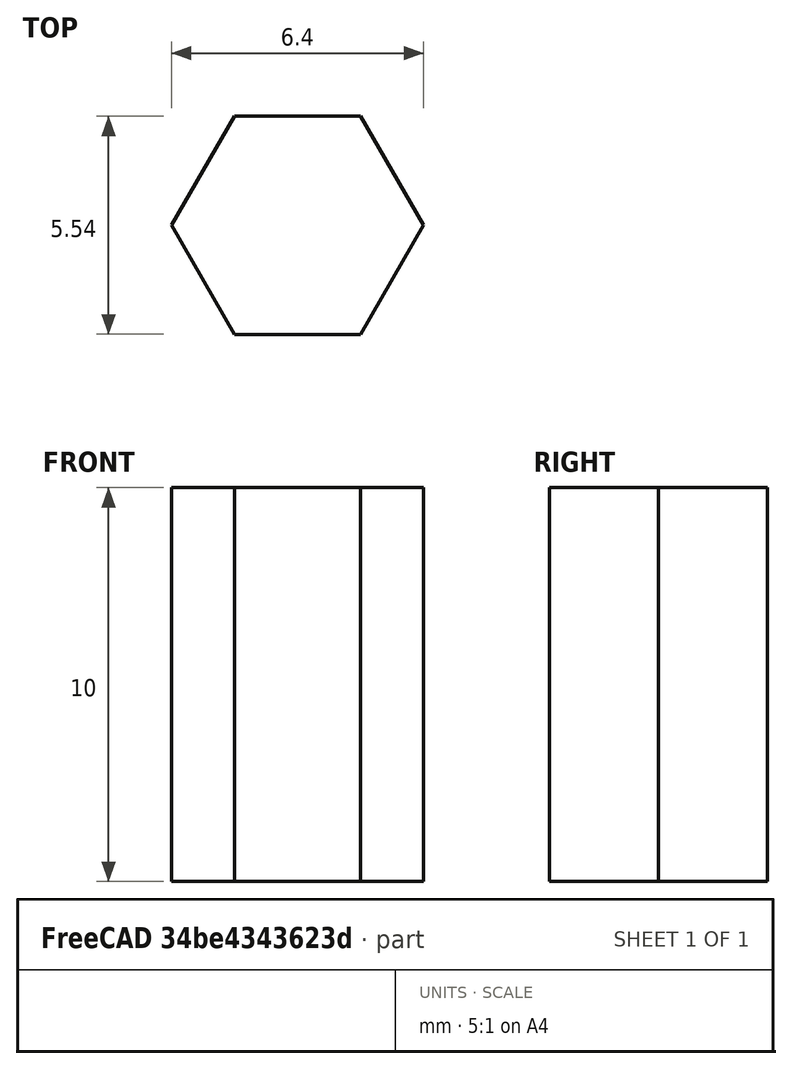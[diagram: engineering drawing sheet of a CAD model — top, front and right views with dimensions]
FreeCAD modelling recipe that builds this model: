
FCSTD DOCUMENT
Label: nut_trap
License: CC-BY 3.0
LicenseURL: http://creativecommons.org/licenses/by/3.0/
objects: Sketcher::SketchObject×1, Part::Extrusion×1
note: 2 computed .brp shape members not serialized (recipe doc carries the construction recipe); baked Part::Feature solids carry a one-line shape summary decoded from their .brp

FEATURE [Sketcher::SketchObject] Sketch
  sketch-geometry (7):
    g0: LineSegment StartX=-1.6 StartY=2.77128 StartZ=0 EndX=1.6 EndY=2.77128 EndZ=0
    g1: LineSegment StartX=1.6 StartY=2.77128 StartZ=0 EndX=3.2 EndY=0 EndZ=0
    g2: LineSegment StartX=3.2 StartY=0 StartZ=0 EndX=1.6 EndY=-2.77128 EndZ=0
    g3: LineSegment StartX=1.6 StartY=-2.77128 StartZ=0 EndX=-1.6 EndY=-2.77128 EndZ=0
    g4: LineSegment StartX=-1.6 StartY=-2.77128 StartZ=0 EndX=-3.2 EndY=0 EndZ=0
    g5: LineSegment StartX=-3.2 StartY=0 StartZ=0 EndX=-1.6 EndY=2.77128 EndZ=0
    g6: GeomPoint [constr] X=0 Y=0 Z=0
  constraints (19):
    c: Coincident(g0,g1)
    c: Coincident(g1,g2)
    c: Coincident(g2,g3)
    c: Coincident(g3,g4)
    c: Coincident(g4,g5)
    c: Coincident(g5,g0)
    c: Distance(g0) = 3.2
    c: Distance(g0,g6) = 3.2
    c: Distance(g0,g6) = 3.2
    c: Distance(g5) = 3.2
    c: Distance(g6,g4) = 3.2
    c: Distance(g3,g4) = 3.2
    c: Distance(g3,g6) = 3.2
    c: Distance(g2,g3) = 3.2
    c: Distance(g2,g6) = 3.2
    c: Distance(g1,g2) = 3.2
    c: Distance(g1,g6) = 3.2
    c: Coincident(g6,g-1)
    c: Horizontal(g0)
FEATURE [Part::Extrusion] Extrude  label="M3NutTrap"
  Base = -> Sketch
  Dir = (0,0,10)
  Solid = true
